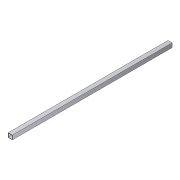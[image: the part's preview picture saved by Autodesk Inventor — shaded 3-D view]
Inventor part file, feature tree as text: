
AUTODESK INVENTOR PART (.ipt)
format: ipt  version: 2012 (Build 160160000, 160)  size: 73,216 bytes
history: native  units: in
note: dims shown in document units (in); Inventor stores cm internally (conversion verified against a paired STEP export)
features: extrude x1, sketch x1
ambient origin geometry x8: Origin, YZ Plane, XZ Plane, XY Plane, X Axis, Y Axis, Z Axis, Center Point
bodies: Solid1 (feature_tree)
feature tree (2):
  extrude  "Extrusion1"  Depth=1.75in
  sketch  "Sketch1"  dims[d0=1.75in d1=1.75in d2=0.125in d3=0.125in d4=0.125in d5=0.125in d6=67.0in d7=0.0in]
